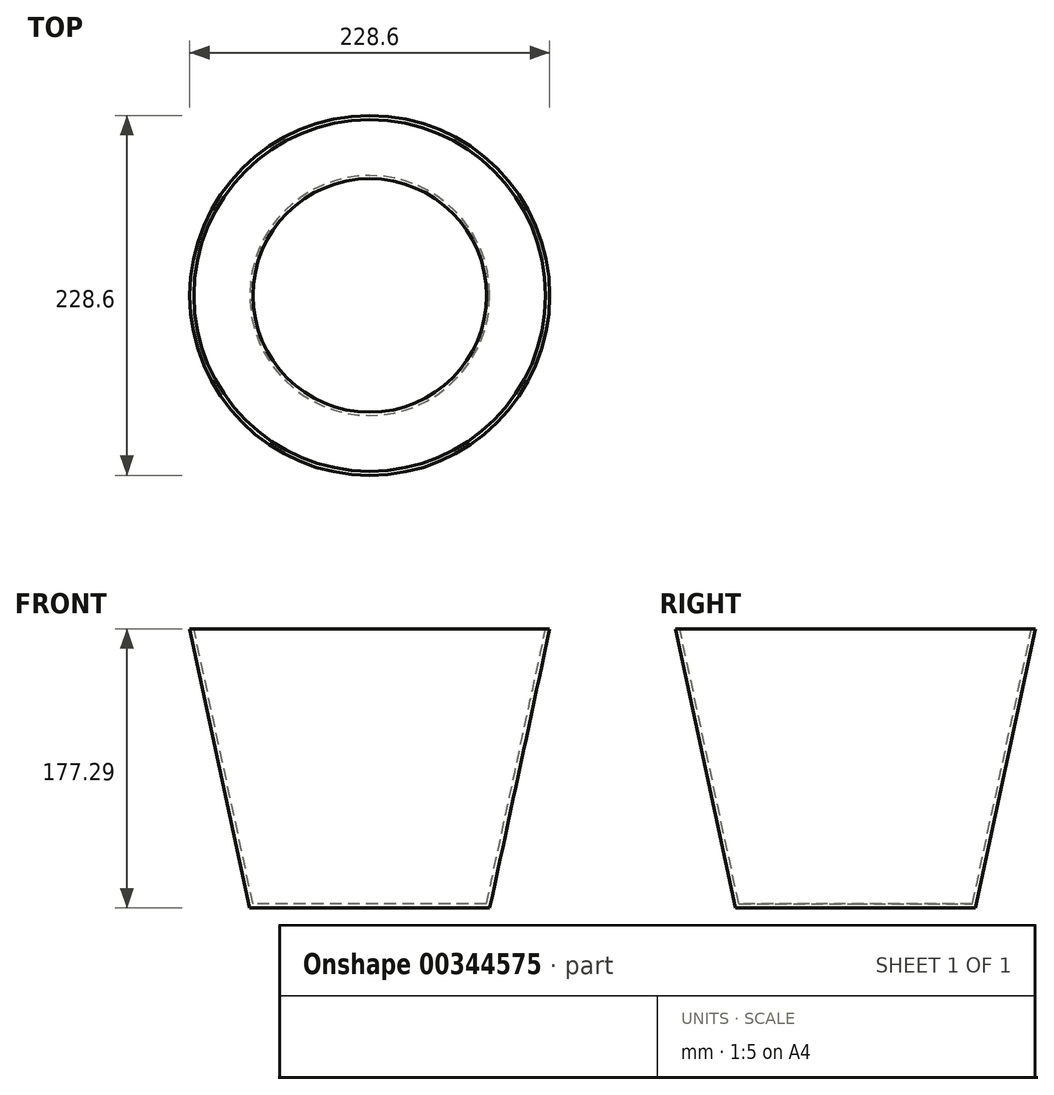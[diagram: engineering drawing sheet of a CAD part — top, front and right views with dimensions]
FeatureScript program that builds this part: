
annotation { "Feature Type Name" : "Feature", "Feature Type Description" : "" }
export const myFeature = defineFeature(function(context is Context, id is Id, definition is map)
    precondition{}
    {
        {
            var Q0;
            Q0=qCreatedBy(makeId("Top.planeOp"),FACE);
            var sketch = newSketch(context, id + "F0", { "sketchPlane" : qUnion([Q0])});
            skCircle(sketch, "E0", {"center": v(0, 0) * mm, "radius": 76.2 * mm});
            skSolve(sketch);
        }
        {
            var Q0;
            Q0=qCreatedBy(makeId("Top.planeOp"),FACE);
            cPlane(context, id + "F1", {"entities" : qUnion([Q0]), "cplaneType" : CPlaneType.OFFSET, "offset" : 177.3 * mm, "width" : 152.4 * mm, "height" : 152.4 * mm});
        }
        {
            var Q0;
            Q0=qCreatedBy(id+"F1.planeOp",FACE);
            var sketch = newSketch(context, id + "F2", { "sketchPlane" : qUnion([Q0])});
            skCircle(sketch, "E1", {"center": v(0, 0) * mm, "radius": 114.3 * mm});
            skSolve(sketch);
        }
        {
            var Q0;
            Q0=makeQuery(id+"F2.imprint","IMPRINT",FACE,{"disambiguationData":[TD([[makeQuery(id+"F2.imprint","IMPRINT",EDGE,{"derivedFrom":sQuery(id+"F2.wireOp",EDGE,"E1")}),1.0]])]});
            var Q1;
            Q1=makeQuery(id+"F0.imprint","IMPRINT",FACE,{"disambiguationData":[TD([[makeQuery(id+"F0.imprint","IMPRINT",EDGE,{"derivedFrom":sQuery(id+"F0.wireOp",EDGE,"E0")}),1.0]])]});
            loft(context, id + "F3", {"sheetProfilesArray" : [{ "sheetProfileEntities" : qUnion([Q0]) }, { "sheetProfileEntities" : qUnion([Q1]) }]});
        }
        {
            var Q0;
            Q0=makeQuery(id+"F3.opLoft","CAP_FACE",FACE,{"disambiguationData":[OSD([makeQuery(id+"F2.imprint","IMPRINT",FACE,{"disambiguationData":[TD([[makeQuery(id+"F2.imprint","IMPRINT",EDGE,{"derivedFrom":sQuery(id+"F2.wireOp",EDGE,"E1")}),1.0]])]})])],"isStart":true});
            shell(context, id + "F4", {"entities" : qUnion([Q0]), "thickness" : 2.54 * mm});
        }
        {
            var Q0;
            Q0=qCreatedBy(makeId("Top.planeOp"),FACE);
            var sketch = newSketch(context, id + "F5", { "sketchPlane" : qUnion([Q0])});
            skLineSegment(sketch, "E2", {"start": v(72.8, 0) * mm, "end": v(-76.72, 0) * mm, "construction": true});
            skSolve(sketch);
        }
        {
            var Q0;
            Q0=qCreatedBy(makeId("Front.planeOp"),FACE);
            var Q1;
            Q1=sQuery(id+"F5.wireOp",EDGE,"E2");
            cPlane(context, id + "F6", {"entities" : qUnion([Q0, Q1]), "cplaneType" : CPlaneType.LINE_ANGLE, "offset" : 25.4 * mm, "angle" : 12.74 * degree, "width" : 152.4 * mm, "height" : 152.4 * mm});
        }
        {
            var Q0;
            Q0=qCreatedBy(id+"F6.planeOp",FACE);
            cPlane(context, id + "F7", {"entities" : qUnion([Q0]), "cplaneType" : CPlaneType.OFFSET, "offset" : 74.68 * mm, "width" : 152.4 * mm, "height" : 152.4 * mm});
        }
    });
